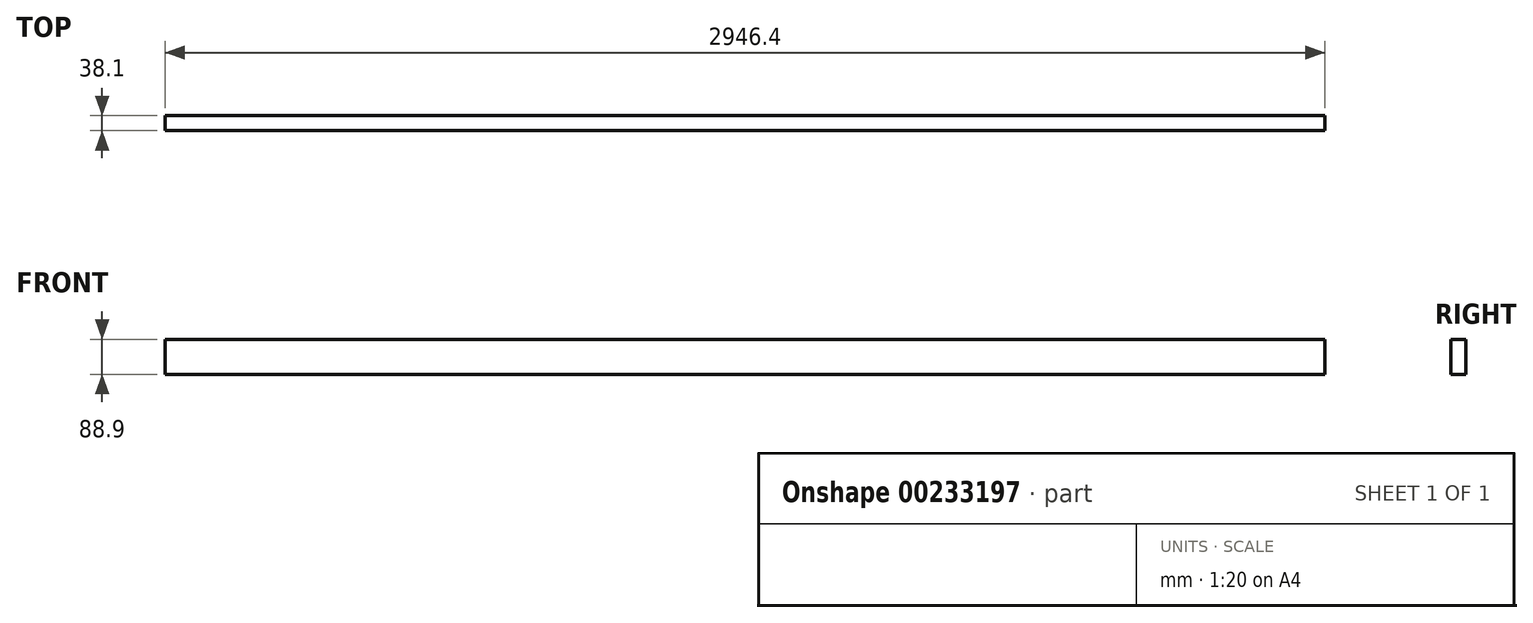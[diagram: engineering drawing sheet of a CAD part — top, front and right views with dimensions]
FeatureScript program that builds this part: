
annotation { "Feature Type Name" : "Feature", "Feature Type Description" : "" }
export const myFeature = defineFeature(function(context is Context, id is Id, definition is map)
    precondition{}
    {
        {
            var Q0;
            Q0=qCreatedBy(makeId("Front.planeOp"),FACE);
            var sketch = newSketch(context, id + "F0", { "sketchPlane" : qUnion([Q0])});
            skLineSegment(sketch, "E0.bottom", {"start": v(-1224.9, 39.3) * mm, "end": v(1721.5, 39.3) * mm});
            skLineSegment(sketch, "E0.top", {"start": v(-1224.9, -49.6) * mm, "end": v(1721.5, -49.6) * mm});
            skLineSegment(sketch, "E0.left", {"start": v(-1224.9, 39.3) * mm, "end": v(-1224.9, -49.6) * mm});
            skLineSegment(sketch, "E0.right", {"start": v(1721.5, 39.3) * mm, "end": v(1721.5, -49.6) * mm});
            skSolve(sketch);
        }
        {
            var Q0;
            Q0 = qSketchRegion(id + "F0", true);
            extrude(context, id + "F1", {"entities" : qUnion([Q0]), "depth" : 38.1 * mm});
        }
    });
